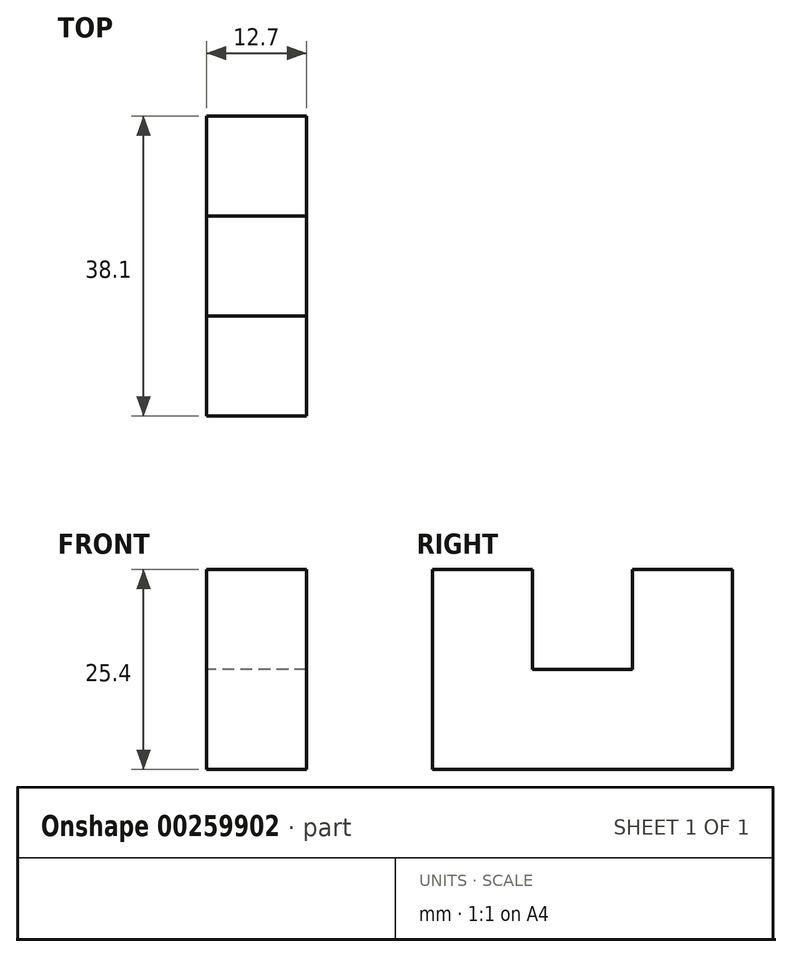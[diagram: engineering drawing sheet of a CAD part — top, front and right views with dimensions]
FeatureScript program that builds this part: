
annotation { "Feature Type Name" : "Feature", "Feature Type Description" : "" }
export const myFeature = defineFeature(function(context is Context, id is Id, definition is map)
    precondition{}
    {
        {
            var Q0;
            Q0=qCreatedBy(makeId("Right.planeOp"),FACE);
            var sketch = newSketch(context, id + "F0", { "sketchPlane" : qUnion([Q0])});
            skLineSegment(sketch, "E0", {"start": v(0, 0) * mm, "end": v(-38.1, 0) * mm});
            skLineSegment(sketch, "E1", {"start": v(-38.1, 0) * mm, "end": v(-38.1, 25.4) * mm});
            skLineSegment(sketch, "E2", {"start": v(-38.1, 25.4) * mm, "end": v(-25.4, 25.4) * mm});
            skLineSegment(sketch, "E3", {"start": v(-25.4, 25.4) * mm, "end": v(-25.4, 12.7) * mm});
            skLineSegment(sketch, "E4", {"start": v(-25.4, 12.7) * mm, "end": v(-12.7, 12.7) * mm});
            skLineSegment(sketch, "E5", {"start": v(-12.7, 12.7) * mm, "end": v(-12.7, 25.4) * mm});
            skLineSegment(sketch, "E6", {"start": v(-12.7, 25.4) * mm, "end": v(0, 25.4) * mm});
            skLineSegment(sketch, "E7", {"start": v(0, 0) * mm, "end": v(0, 25.4) * mm});
            skSolve(sketch);
        }
        {
            var Q0;
            {var subQ0=sQuery(id+"F0.wireOp",EDGE,"E1");Q0=makeQuery(id+"F0.imprint","IMPRINT",FACE,{"disambiguationData":[TD([[makeQuery(id+"F0.imprint","IMPRINT",EDGE,{"derivedFrom":subQ0}),-1.0]])]});}
            extrude(context, id + "F1", {"entities" : qUnion([Q0]), "depth" : 12.7 * mm});
        }
    });
